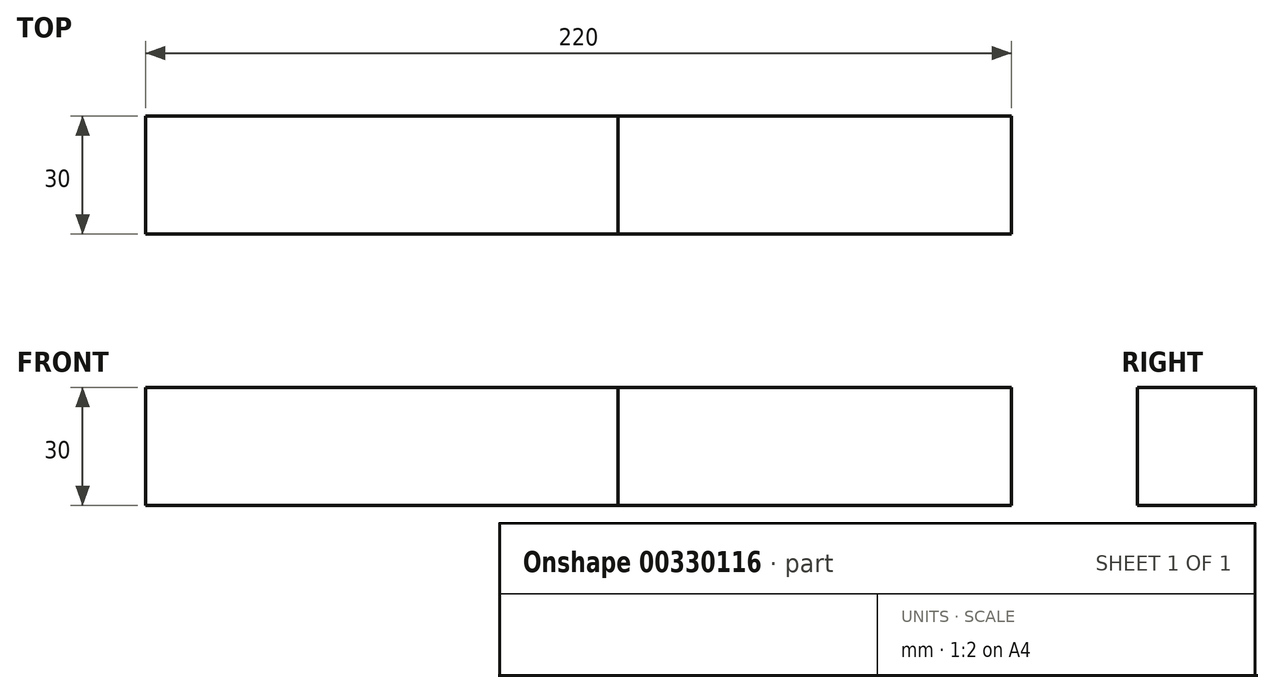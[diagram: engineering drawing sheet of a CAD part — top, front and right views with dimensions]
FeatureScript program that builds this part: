
annotation { "Feature Type Name" : "Feature", "Feature Type Description" : "" }
export const myFeature = defineFeature(function(context is Context, id is Id, definition is map)
    precondition{}
    {
        {
            var Q0;
            Q0=qCreatedBy(makeId("Right.planeOp"),FACE);
            cPlane(context, id + "F0", {"entities" : qUnion([Q0]), "cplaneType" : CPlaneType.OFFSET, "offset" : 60 * mm, "width" : 150 * mm, "height" : 150 * mm});
        }
        {
            var Q0;
            Q0=qCreatedBy(makeId("Front.planeOp"),FACE);
            var sketch = newSketch(context, id + "F1", { "sketchPlane" : qUnion([Q0])});
            skLineSegment(sketch, "E0.bottom", {"start": v(60, 0) * mm, "end": v(160, 0) * mm});
            skLineSegment(sketch, "E0.top", {"start": v(60, -30) * mm, "end": v(160, -30) * mm});
            skLineSegment(sketch, "E0.left", {"start": v(60, 0) * mm, "end": v(60, -30) * mm});
            skLineSegment(sketch, "E0.right", {"start": v(160, 0) * mm, "end": v(160, -30) * mm});
            skLineSegment(sketch, "E1.bottom", {"start": v(60, 0) * mm, "end": v(-60, 0) * mm});
            skLineSegment(sketch, "E1.top", {"start": v(60, -30) * mm, "end": v(-60, -30) * mm});
            skLineSegment(sketch, "E1.right", {"start": v(-60, 0) * mm, "end": v(-60, -30) * mm});
            skLineSegment(sketch, "E2", {"start": v(60, 61) * mm, "end": v(60, -61) * mm, "construction": true});
            skSolve(sketch);
        }
        {
            var Q0;
            Q0=qCreatedBy(makeId("Front.planeOp"),FACE);
            cPlane(context, id + "F2", {"entities" : qUnion([Q0]), "cplaneType" : CPlaneType.OFFSET, "offset" : 30 * mm, "width" : 150 * mm, "height" : 150 * mm});
        }
        {
            var Q0;
            Q0=makeQuery(id+"F1.imprint","IMPRINT",FACE,{"disambiguationData":[TD([[makeQuery(id+"F1.imprint","IMPRINT",EDGE,{"derivedFrom":sQuery(id+"F1.wireOp",EDGE,"E1.bottom")}),1.0]])]});
            var Q1;
            Q1=qCreatedBy(id+"F2.planeOp",FACE);
            extrude(context, id + "F3", {"entities" : qUnion([Q0]), "endBound" : BoundingType.UP_TO_SURFACE, "endBoundEntityFace" : qUnion([Q1]), "depth" : 50 * mm});
        }
        {
            var Q0;
            Q0=makeQuery(id+"F1.imprint","IMPRINT",FACE,{"disambiguationData":[TD([[makeQuery(id+"F1.imprint","IMPRINT",EDGE,{"derivedFrom":sQuery(id+"F1.wireOp",EDGE,"E0.bottom")}),-1.0]])]});
            var Q1;
            Q1=qCreatedBy(id+"F2.planeOp",FACE);
            extrude(context, id + "F4", {"entities" : qUnion([Q0]), "endBound" : BoundingType.UP_TO_SURFACE, "endBoundEntityFace" : qUnion([Q1]), "depth" : 25 * mm});
        }
    });
